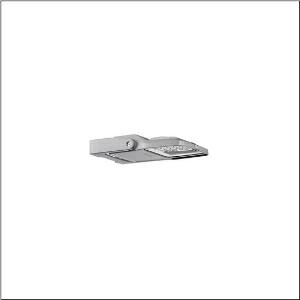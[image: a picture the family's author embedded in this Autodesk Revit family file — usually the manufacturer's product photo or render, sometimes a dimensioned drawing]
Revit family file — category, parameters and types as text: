
# Revit family: floodlight_fl_21_iq_micro___pl52_5xa7762a4d2a_e4f8
name_source: partatom
category: Lighting Fixtures
units: mm (PartAtom-declared; Revit-internal decimal feet)

## family parameters
Cut with Voids When Loaded = No
Host = Face
Light Source = No
Part Type = Normal
Room Calculation Point = No
Round Connector Dimension = Use Diameter
Shared = No

## types (1)
- --- (1 x LED, 3010 lm, 23.1 W, 4000K)
    Apparent Load = 23 VA
    CIE Flux Codes = 26 60 98 100 100
    Color Rendering = 70
    Color Temperature = 4000K
    Default Elevation = 1800 mm
    Description = Floodlight FL 21 iQ micro, floodlight, primary light control with lens, of PMMA, primary optical cover: protective disc, of toughened safety glass, transparent, light distribution: PL52, light emission: direct distribution, installation type: surface-mounted, lamps: LED, High Power LED, rated values: 3.010lm | 23,1W | 130,3lm/W (begin service life); end service life: 3.010lm | 23,8W; at 50% lumin. flux: 1.505lm | 11W | 136,8lm/W, colour temperature: 4000K, colour rendering: CRI > 70, light colour: 740, light setting 1 begin service life: 100% | 3.010lm | 23,1W | 130,3lm/W | 4.000K, light setting 1 end service life: 23,8W, further light settings possible, control: Auto-Match, Temp-Guard, Night-Set, Smart-Wire, Desk-Remote (wireless, voltage-free reading and setting of iQ features in the workshop via application-optimized NFC function/RFID function), optimised constant luminous flux control (CLO 2.0), Street-Remote, pre-setting: linear dimming characteristic, with terminal, 6-pole, mains connection: 220..240V, AC, 50/60Hz, luminaire housing, of diecast aluminium, powder-coated, SITECO metallic grey (DB 702S), corrosivity category C5 mid according to DIN EN ISO 12944suitable for swimming poolschlorine-resistant, sealing non-destructively replaceable, design bracket, of diecast aluminium, powder-coated, SITECO metallic grey (DB 702S), protection rating (complete): IP66, insulation class (complete): insulation class II (safety insulation), certification: CE, ENEC, VDE, protection symbol: D, impact resistance: IK07, permissible operating ambient temperature: -40..+40°C, permissible operating ambient temperature for outdoor applications: -40..+50°C, standard: DIN EN 12944, LABS conformity tested according to VDMA 24364:2018-05, packaging unit: 1 piece

Light Distribution: PL52
    Height = 65 mm
    Lamp = 1 x LED
    Lamp Light Flux = 3010 lm
    Lamp Power = 23.1 W
    Lamp count = 1
    Length = 312 mm
    Luminous efficacy = 130 lm/W
    Manufacturer = Siteco
    ModVariant = No
    Model = 5XA7762A4D2A
    Mounting Place = Wall
    Mounting Type = Surface mounted
    Number of Poles = 1
    OnlyDefault = Yes
    Power Factor = 1
    Product Name = Floodlight FL 21 iQ micro | PL52
    Product group = floodlight | wall mounted
    ProductGroupID = 2002
    Protection Class = Protection class II
    Protection Degree = IP 66
    RLX_Detail_Level = 1
    RLX_Emergency_Light_Flux = 0 lm
    RLX_Emergency_Type = 0
    RLX_Emergency_Type_DB = No
    RlxData = <blob elided: 97833 chars, md5=710bf437>
    Socket = socket
    Standby Power = 0 W
    System Light Flux = 3010 lm
    System Power = 23 W
    Type Comments = factory setting: luminous flux: 100 % | dim-lin: 254 | 455 mA
    Type Image = l_1006878.jpg
    URL = http://relux.com
    VarID = @adj_178811
    Voltage = 0 V
    Weight = 0.00 kg
    Width = 230 mm

## geometry (parser evidence)
native form markers: Blend x4, Sweep x10
no freeform markers — native parametric forms only
